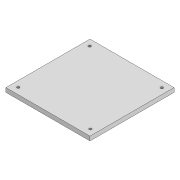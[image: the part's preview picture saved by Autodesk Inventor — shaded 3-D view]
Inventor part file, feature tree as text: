
AUTODESK INVENTOR PART (.ipt)
format: ipt  version: 2020 (Build 240168000, 168)  size: 113,664 bytes
history: native  units: mm
features: extrude x2, sketch x2
ambient origin geometry x8: Origin, YZ Plane, XZ Plane, XY Plane, X Axis, Y Axis, Z Axis, Center Point
bodies: Solid1 (feature_tree)
feature tree (4):
  extrude  "Extrusion1"  Depth=100.0mm
  extrude  "Extrusion2"  Depth=5.0mm
  sketch  "Sketch1"  dims[d0=100.0mm d1=100.0mm]
  sketch  "Sketch2"  dims[d2=85.8mm d3=85.0mm d4=3.0mm d5=3.0mm d6=3.0mm d7=3.0mm d8=5.0mm d9=0.0mm d10=40.0mm d11=3.0mm d12=40.0mm d13=3.0mm d14=5.0mm d15=0.0mm]
